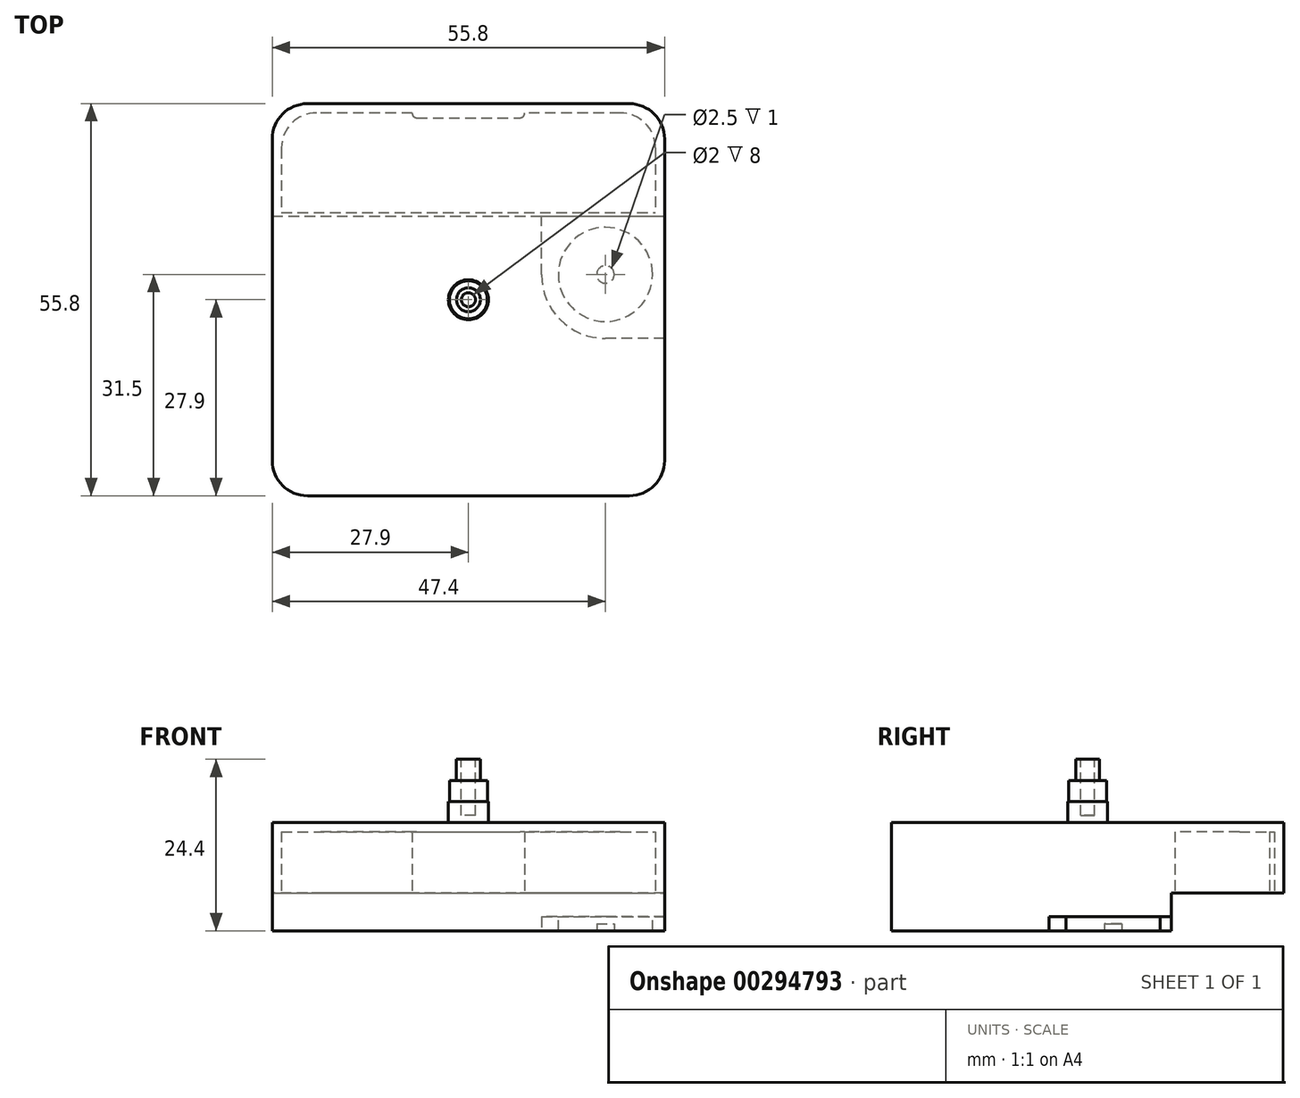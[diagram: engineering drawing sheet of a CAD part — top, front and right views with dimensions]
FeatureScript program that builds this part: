
annotation { "Feature Type Name" : "Feature", "Feature Type Description" : "" }
export const myFeature = defineFeature(function(context is Context, id is Id, definition is map)
    precondition{}
    {
        {
            var Q0;
            Q0=qCreatedBy(makeId("Top.planeOp"),FACE);
            var sketch = newSketch(context, id + "F0", { "sketchPlane" : qUnion([Q0])});
            skLineSegment(sketch, "E0.bottom", {"start": v(22.9, -27.9) * mm, "end": v(-22.9, -27.9) * mm});
            skLineSegment(sketch, "E0.top", {"start": v(22.9, 27.9) * mm, "end": v(-22.9, 27.9) * mm});
            skLineSegment(sketch, "E0.left", {"start": v(27.9, -22.9) * mm, "end": v(27.9, 22.9) * mm});
            skLineSegment(sketch, "E0.right", {"start": v(-27.9, -22.9) * mm, "end": v(-27.9, 22.9) * mm});
            skPoint(sketch, "E0.middle", {"position": v(0, 0) * mm});
            skPoint(sketch, "E1.visualSharp", {"position": v(-27.9, -27.9) * mm});
            skArc(sketch, "E1.filletArc", {"start": v(-27.9, -22.9) * mm, "mid": v(-26.44, -26.44) * mm, "end": v(-22.9, -27.9) * mm});
            skPoint(sketch, "E2.visualSharp", {"position": v(27.9, -27.9) * mm});
            skArc(sketch, "E2.filletArc", {"start": v(22.9, -27.9) * mm, "mid": v(26.44, -26.44) * mm, "end": v(27.9, -22.9) * mm});
            skPoint(sketch, "E3.visualSharp", {"position": v(27.9, 27.9) * mm});
            skArc(sketch, "E3.filletArc", {"start": v(27.9, 22.9) * mm, "mid": v(26.44, 26.44) * mm, "end": v(22.9, 27.9) * mm});
            skPoint(sketch, "E4.visualSharp", {"position": v(-27.9, 27.9) * mm});
            skArc(sketch, "E4.filletArc", {"start": v(-22.9, 27.9) * mm, "mid": v(-26.44, 26.44) * mm, "end": v(-27.9, 22.9) * mm});
            skSolve(sketch);
        }
        {
            var Q0;
            Q0=makeQuery(id+"F0.imprint","IMPRINT",FACE,{"disambiguationData":[TD([[makeQuery(id+"F0.imprint","IMPRINT",EDGE,{"derivedFrom":sQuery(id+"F0.wireOp",EDGE,"E0.bottom")}),-1.0]])]});
            extrude(context, id + "F1", {"entities" : qUnion([Q0]), "depth" : 15.4 * mm});
        }
        {
            var Q0;
            Q0=makeQuery(id+"F1.opExtrude","CAP_FACE",FACE,{"disambiguationData":[OSD([sQuery(id+"F0.wireOp",EDGE,"E0.bottom"),sQuery(id+"F0.wireOp",EDGE,"E0.top"),sQuery(id+"F0.wireOp",EDGE,"E0.left"),sQuery(id+"F0.wireOp",EDGE,"E0.right"),sQuery(id+"F0.wireOp",EDGE,"E1.filletArc"),sQuery(id+"F0.wireOp",EDGE,"E2.filletArc"),sQuery(id+"F0.wireOp",EDGE,"E3.filletArc"),sQuery(id+"F0.wireOp",EDGE,"E4.filletArc")])],"isStart":true});
            var sketch = newSketch(context, id + "F2", { "sketchPlane" : qUnion([Q0])});
            skLineSegment(sketch, "E5", {"start": v(-27.9, -11.9) * mm, "end": v(27.9, -11.9) * mm});
            skLineSegment(sketch, "E6", {"start": v(-27.9, -11.9) * mm, "end": v(-27.9, -27.9) * mm});
            skLineSegment(sketch, "E7", {"start": v(-27.9, -27.9) * mm, "end": v(27.9, -27.9) * mm});
            skLineSegment(sketch, "E8", {"start": v(27.9, -27.9) * mm, "end": v(27.9, -11.9) * mm});
            skSolve(sketch);
        }
        {
            var Q0;
            {var subQ4=sQuery(id+"F2.wireOp",EDGE,"E5");Q0=makeQuery(id+"F2.imprint","IMPRINT",FACE,{"disambiguationData":[TD([[makeQuery(id+"F2.imprint","IMPRINT",EDGE,{"derivedFrom":subQ4}),-1.0]])]});}
            extrude(context, id + "F3", {"entities" : qUnion([Q0]), "operationType" : NewBodyOperationType.REMOVE, "oppositeDirection" : true, "depth" : 5.4 * mm});
        }
        {
            var Q0;
            Q0=makeQuery(id+"F1.opExtrude","CAP_FACE",FACE,{"disambiguationData":[OSD([sQuery(id+"F0.wireOp",EDGE,"E0.bottom"),sQuery(id+"F0.wireOp",EDGE,"E0.top"),sQuery(id+"F0.wireOp",EDGE,"E0.left"),sQuery(id+"F0.wireOp",EDGE,"E0.right"),sQuery(id+"F0.wireOp",EDGE,"E1.filletArc"),sQuery(id+"F0.wireOp",EDGE,"E2.filletArc"),sQuery(id+"F0.wireOp",EDGE,"E3.filletArc"),sQuery(id+"F0.wireOp",EDGE,"E4.filletArc")])],"isStart":true});
            var sketch = newSketch(context, id + "F4", { "sketchPlane" : qUnion([Q0])});
            skLineSegment(sketch, "E9", {"start": v(27.9, 5.5) * mm, "end": v(19.5, 5.5) * mm});
            skLineSegment(sketch, "E10", {"start": v(10.4, -3.6) * mm, "end": v(10.4, -11.9) * mm});
            skLineSegment(sketch, "E11", {"start": v(10.4, -11.9) * mm, "end": v(27.9, -11.9) * mm});
            skLineSegment(sketch, "E12", {"start": v(27.9, -11.9) * mm, "end": v(27.9, 5.5) * mm});
            skPoint(sketch, "E13.visualSharp", {"position": v(10.4, 5.5) * mm});
            skArc(sketch, "E13.filletArc", {"start": v(19.5, 5.5) * mm, "mid": v(13.07, 2.83) * mm, "end": v(10.4, -3.6) * mm});
            skSolve(sketch);
        }
        {
            var Q0;
            Q0 = qSketchRegion(id + "F4", true);
            extrude(context, id + "F5", {"entities" : qUnion([Q0]), "operationType" : NewBodyOperationType.REMOVE, "oppositeDirection" : true, "depth" : 2 * mm});
        }
        {
            var Q0;
            Q0=makeQuery(id+"F5.boolean.opBoolean","COPY",FACE,{"derivedFrom":makeQuery(id+"F5.opExtrude","CAP_FACE",FACE,{"disambiguationData":[OSD([sQuery(id+"F4.wireOp",EDGE,"E9"),sQuery(id+"F4.wireOp",EDGE,"E10"),sQuery(id+"F4.wireOp",EDGE,"E11"),sQuery(id+"F4.wireOp",EDGE,"E12"),sQuery(id+"F4.wireOp",EDGE,"E13.filletArc")])],"isStart":false})});
            var sketch = newSketch(context, id + "F6", { "sketchPlane" : qUnion([Q0])});
            skCircle(sketch, "E14", {"center": v(19.5, -3.6) * mm, "radius": 6.7 * mm});
            skSolve(sketch);
        }
        {
            var Q0;
            Q0 = qSketchRegion(id + "F6", true);
            extrude(context, id + "F7", {"entities" : qUnion([Q0]), "operationType" : NewBodyOperationType.ADD, "depth" : 2 * mm});
        }
        {
            var Q0;
            Q0=makeQuery(id+"F3.boolean.opBoolean","COPY",FACE,{"derivedFrom":makeQuery(id+"F3.opExtrude","CAP_FACE",FACE,{"disambiguationData":[OSD([sQuery(id+"F0.wireOp",EDGE,"E3.filletArc"),sQuery(id+"F0.wireOp",EDGE,"E4.filletArc"),sQuery(id+"F2.wireOp",EDGE,"E5"),sQuery(id+"F2.wireOp",EDGE,"E6"),sQuery(id+"F2.wireOp",EDGE,"E7"),sQuery(id+"F2.wireOp",EDGE,"E8")])],"isStart":false})});
            var sketch = newSketch(context, id + "F8", { "sketchPlane" : qUnion([Q0])});
            skLineSegment(sketch, "E15", {"start": v(21.6, -26.6) * mm, "end": v(8, -26.6) * mm});
            skLineSegment(sketch, "E16", {"start": v(-26.6, -21.6) * mm, "end": v(-26.6, -12.4) * mm});
            skLineSegment(sketch, "E17", {"start": v(-26.6, -12.4) * mm, "end": v(26.6, -12.4) * mm});
            skLineSegment(sketch, "E18", {"start": v(26.6, -21.6) * mm, "end": v(26.6, -12.4) * mm});
            skPoint(sketch, "E19.visualSharp", {"position": v(-26.6, -26.6) * mm});
            skArc(sketch, "E19.filletArc", {"start": v(-26.6, -21.6) * mm, "mid": v(-25.14, -25.14) * mm, "end": v(-21.6, -26.6) * mm});
            skPoint(sketch, "E20.visualSharp", {"position": v(26.6, -26.6) * mm});
            skArc(sketch, "E20.filletArc", {"start": v(21.6, -26.6) * mm, "mid": v(25.14, -25.14) * mm, "end": v(26.6, -21.6) * mm});
            skLineSegment(sketch, "E21", {"start": v(-8, -26.6) * mm, "end": v(-8, -26.55) * mm});
            skLineSegment(sketch, "E22", {"start": v(-7.35, -25.9) * mm, "end": v(7.35, -25.9) * mm});
            skLineSegment(sketch, "E23", {"start": v(8, -26.55) * mm, "end": v(8, -26.6) * mm});
            skPoint(sketch, "E24", {"position": v(0, -25.9) * mm});
            skLineSegment(sketch, "E25.trimOffspring", {"start": v(-8, -26.6) * mm, "end": v(-21.6, -26.6) * mm});
            skPoint(sketch, "E26.visualSharp", {"position": v(-8, -25.9) * mm});
            skArc(sketch, "E26.filletArc", {"start": v(-7.35, -25.9) * mm, "mid": v(-7.8, -26.1) * mm, "end": v(-8, -26.55) * mm});
            skPoint(sketch, "E27.visualSharp", {"position": v(8, -25.9) * mm});
            skArc(sketch, "E27.filletArc", {"start": v(8, -26.55) * mm, "mid": v(7.8, -26.1) * mm, "end": v(7.35, -25.9) * mm});
            skSolve(sketch);
        }
        {
            var Q0;
            Q0=makeQuery(id+"F8.imprint","IMPRINT",FACE,{"disambiguationData":[TD([[makeQuery(id+"F8.imprint","IMPRINT",EDGE,{"derivedFrom":sQuery(id+"F8.wireOp",EDGE,"E15")}),-1.0]])]});
            extrude(context, id + "F9", {"entities" : qUnion([Q0]), "operationType" : NewBodyOperationType.REMOVE, "oppositeDirection" : true, "depth" : (10 - 1.3) * mm});
        }
        {
            var Q0;
            Q0=makeQuery(id+"F7.opExtrude","CAP_FACE",FACE,{"disambiguationData":[OSD([sQuery(id+"F6.wireOp",EDGE,"E14")])],"isStart":false});
            var sketch = newSketch(context, id + "F10", { "sketchPlane" : qUnion([Q0])});
            skCircle(sketch, "E28", {"center": v(19.5, -3.6) * mm, "radius": 1.25 * mm});
            skSolve(sketch);
        }
        {
            var Q0;
            Q0 = qSketchRegion(id + "F10", true);
            extrude(context, id + "F11", {"entities" : qUnion([Q0]), "operationType" : NewBodyOperationType.REMOVE, "oppositeDirection" : true, "depth" : 1 * mm});
        }
        {
            var Q0;
            Q0=makeQuery(id+"F1.opExtrude","CAP_FACE",FACE,{"disambiguationData":[OSD([sQuery(id+"F0.wireOp",EDGE,"E0.bottom"),sQuery(id+"F0.wireOp",EDGE,"E0.top"),sQuery(id+"F0.wireOp",EDGE,"E0.left"),sQuery(id+"F0.wireOp",EDGE,"E0.right"),sQuery(id+"F0.wireOp",EDGE,"E1.filletArc"),sQuery(id+"F0.wireOp",EDGE,"E2.filletArc"),sQuery(id+"F0.wireOp",EDGE,"E3.filletArc"),sQuery(id+"F0.wireOp",EDGE,"E4.filletArc")])],"isStart":false});
            var sketch = newSketch(context, id + "F12", { "sketchPlane" : qUnion([Q0])});
            skCircle(sketch, "E29", {"center": v(0, 0) * mm, "radius": 2.85 * mm});
            skSolve(sketch);
        }
        {
            var Q0;
            Q0 = qSketchRegion(id + "F12", true);
            extrude(context, id + "F13", {"entities" : qUnion([Q0]), "operationType" : NewBodyOperationType.ADD, "depth" : 3 * mm});
        }
        {
            var Q0;
            Q0=makeQuery(id+"F13.opExtrude","CAP_FACE",FACE,{"disambiguationData":[OSD([sQuery(id+"F12.wireOp",EDGE,"E29")])],"isStart":false});
            var sketch = newSketch(context, id + "F14", { "sketchPlane" : qUnion([Q0])});
            skCircle(sketch, "E30", {"center": v(0, 0) * mm, "radius": 2.7 * mm});
            skSolve(sketch);
        }
        {
            var Q0;
            Q0 = qSketchRegion(id + "F14", true);
            extrude(context, id + "F15", {"entities" : qUnion([Q0]), "operationType" : NewBodyOperationType.ADD, "depth" : 3 * mm});
        }
        {
            var Q0;
            Q0=makeQuery(id+"F15.opExtrude","CAP_FACE",FACE,{"disambiguationData":[OSD([sQuery(id+"F14.wireOp",EDGE,"E30")])],"isStart":false});
            var sketch = newSketch(context, id + "F16", { "sketchPlane" : qUnion([Q0])});
            skCircle(sketch, "E31", {"center": v(0, 0) * mm, "radius": 1 * mm});
            skSolve(sketch);
        }
        {
            var Q0;
            Q0 = qSketchRegion(id + "F16", true);
            extrude(context, id + "F17", {"entities" : qUnion([Q0]), "operationType" : NewBodyOperationType.REMOVE, "oppositeDirection" : true, "depth" : 5 * mm});
        }
        {
            var Q0;
            Q0=makeQuery(id+"F15.opExtrude","CAP_FACE",FACE,{"disambiguationData":[OSD([sQuery(id+"F14.wireOp",EDGE,"E30")])],"isStart":false});
            var sketch = newSketch(context, id + "F18", { "sketchPlane" : qUnion([Q0])});
            skCircle(sketch, "E32", {"center": v(0, 0) * mm, "radius": 1.7 * mm});
            skSolve(sketch);
        }
        {
            var Q0;
            Q0=makeQuery(id+"F18.imprint","IMPRINT",FACE,{"disambiguationData":[TD([[makeQuery(id+"F18.imprint","IMPRINT",EDGE,{"derivedFrom":sQuery(id+"F18.wireOp",EDGE,"E32")}),1.0]])]});
            extrude(context, id + "F19", {"entities" : qUnion([Q0]), "operationType" : NewBodyOperationType.ADD, "depth" : 3 * mm});
        }
    });
